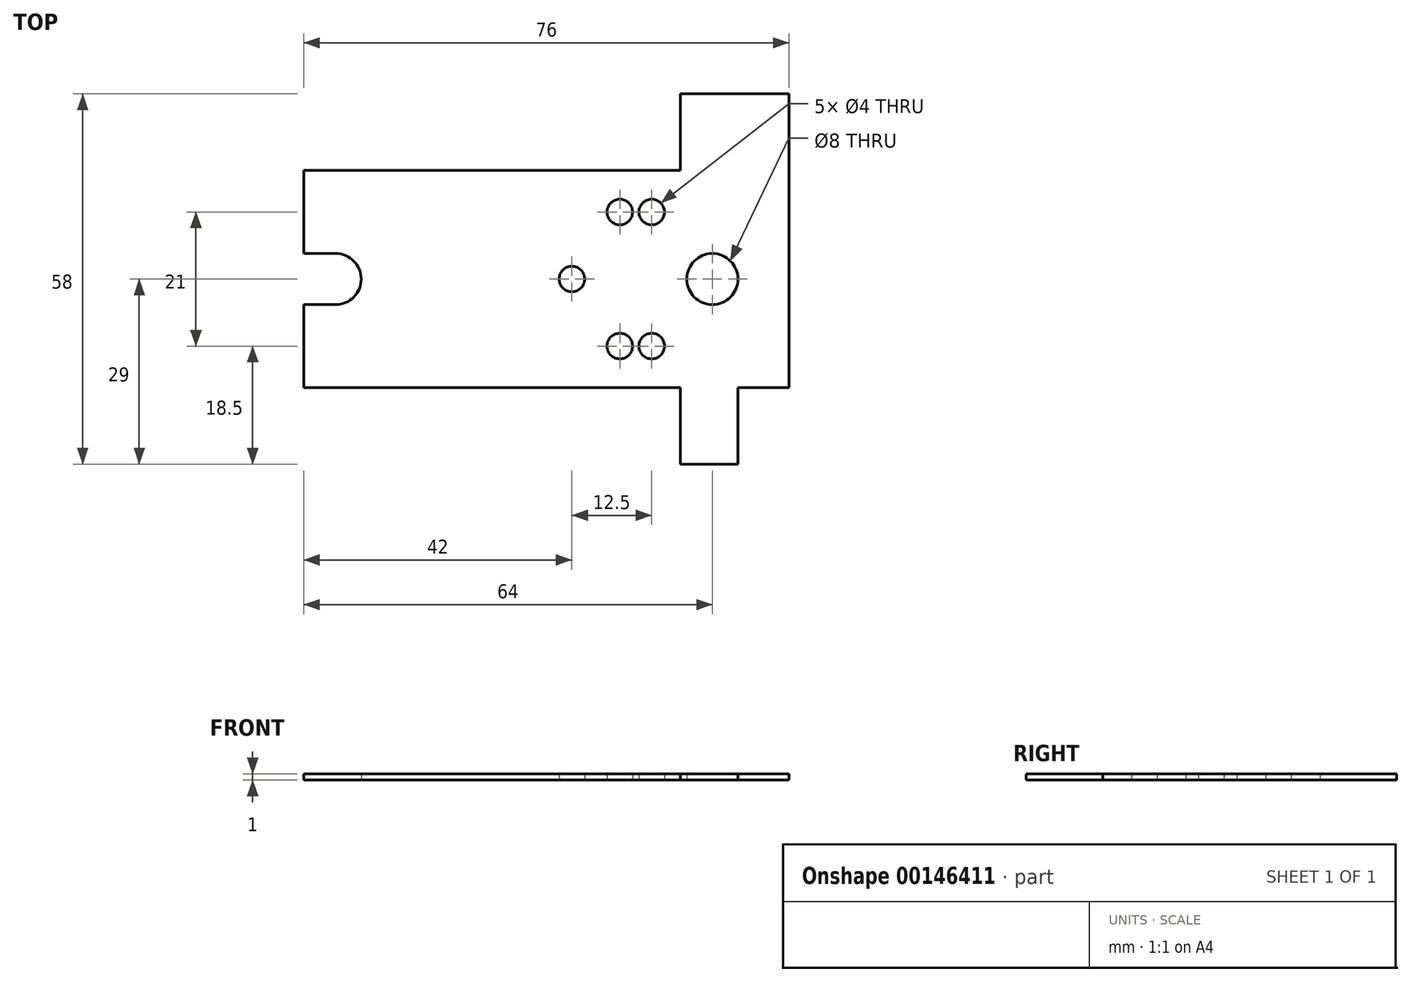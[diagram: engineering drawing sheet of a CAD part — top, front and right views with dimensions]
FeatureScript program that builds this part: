
annotation { "Feature Type Name" : "Feature", "Feature Type Description" : "" }
export const myFeature = defineFeature(function(context is Context, id is Id, definition is map)
    precondition{}
    {
        {
            var Q0;
            Q0=qCreatedBy(makeId("Top.planeOp"),FACE);
            var sketch = newSketch(context, id + "F0", { "sketchPlane" : qUnion([Q0])});
            skLineSegment(sketch, "E0.bottom", {"start": v(0, 0) * mm, "end": v(17, 0) * mm});
            skLineSegment(sketch, "E0.top", {"start": v(0, 34) * mm, "end": v(17, 34) * mm});
            skLineSegment(sketch, "E0.left", {"start": v(0, 0) * mm, "end": v(0, 34) * mm});
            skLineSegment(sketch, "E0.right", {"start": v(17, 0) * mm, "end": v(17, 34) * mm});
            skCircle(sketch, "E1", {"center": v(5, 17) * mm, "radius": 4 * mm});
            skPoint(sketch, "E2.positionSnap0", {"position": v(17, 17) * mm});
            skLineSegment(sketch, "E3.bottom", {"start": v(0, 34) * mm, "end": v(-12, 34) * mm});
            skLineSegment(sketch, "E3.top", {"start": v(0, 0) * mm, "end": v(-12, 0) * mm});
            skLineSegment(sketch, "E3.left", {"start": v(0, 34) * mm, "end": v(0, 0) * mm});
            skLineSegment(sketch, "E3.right", {"start": v(-12, 34) * mm, "end": v(-12, 0) * mm});
            skLineSegment(sketch, "E4.bottom", {"start": v(-12, 34) * mm, "end": v(-29, 34) * mm});
            skLineSegment(sketch, "E4.top", {"start": v(-12, 0) * mm, "end": v(-29, 0) * mm});
            skLineSegment(sketch, "E4.right", {"start": v(-29, 34) * mm, "end": v(-29, 0) * mm});
            skCircle(sketch, "E5", {"center": v(-17, 17) * mm, "radius": 2 * mm});
            skLineSegment(sketch, "E6", {"start": v(-19, 17) * mm, "end": v(-50, 17) * mm});
            skLineSegment(sketch, "E7.bottom", {"start": v(-4.5, 27.5) * mm, "end": v(-9.5, 27.5) * mm, "construction": true});
            skLineSegment(sketch, "E7.top", {"start": v(-4.5, 6.5) * mm, "end": v(-9.5, 6.5) * mm, "construction": true});
            skLineSegment(sketch, "E7.left", {"start": v(-4.5, 27.5) * mm, "end": v(-4.5, 6.5) * mm, "construction": true});
            skLineSegment(sketch, "E7.right", {"start": v(-9.5, 27.5) * mm, "end": v(-9.5, 6.5) * mm, "construction": true});
            skPoint(sketch, "E7.middle", {"position": v(-7, 17) * mm});
            skCircle(sketch, "E8", {"center": v(-4.5, 27.5) * mm, "radius": 2 * mm});
            skCircle(sketch, "E9", {"center": v(-9.5, 27.5) * mm, "radius": 2 * mm});
            skCircle(sketch, "E10", {"center": v(-9.5, 6.5) * mm, "radius": 2 * mm});
            skCircle(sketch, "E11", {"center": v(-4.5, 6.5) * mm, "radius": 2 * mm});
            skLineSegment(sketch, "E12.top", {"start": v(0, 46) * mm, "end": v(17, 46) * mm});
            skLineSegment(sketch, "E12.left", {"start": v(0, 34) * mm, "end": v(0, 46) * mm});
            skLineSegment(sketch, "E12.right", {"start": v(17, 34) * mm, "end": v(17, 46) * mm});
            skLineSegment(sketch, "E13.top", {"start": v(0, -12) * mm, "end": v(9, -12) * mm});
            skLineSegment(sketch, "E13.left", {"start": v(0, 0) * mm, "end": v(0, -12) * mm});
            skLineSegment(sketch, "E13.right", {"start": v(9, 0) * mm, "end": v(9, -12) * mm});
            skLineSegment(sketch, "E14.bottom", {"start": v(-29, 34) * mm, "end": v(-42, 34) * mm});
            skLineSegment(sketch, "E14.top", {"start": v(-29, 0) * mm, "end": v(-42, 0) * mm});
            skLineSegment(sketch, "E14.right", {"start": v(-42, 34) * mm, "end": v(-42, 0) * mm});
            skLineSegment(sketch, "E15.bottom", {"start": v(-42, 34) * mm, "end": v(-59, 34) * mm});
            skLineSegment(sketch, "E15.top", {"start": v(-42, 0) * mm, "end": v(-59, 0) * mm});
            skLineSegment(sketch, "E15.right", {"start": v(-59, 34) * mm, "end": v(-59, 21) * mm});
            skArc(sketch, "E16", {"start": v(-54, 13) * mm, "mid": v(-50, 17) * mm, "end": v(-54, 21) * mm});
            skLineSegment(sketch, "E17", {"start": v(-54, 13) * mm, "end": v(-59, 13) * mm});
            skLineSegment(sketch, "E18", {"start": v(-54, 21) * mm, "end": v(-59, 21) * mm});
            skLineSegment(sketch, "E19.trimOffspring", {"start": v(-59, 13) * mm, "end": v(-59, 0) * mm});
            skSolve(sketch);
        }
        {
            var Q0;
            {var subQ4=sQuery(id+"F0.wireOp",EDGE,"E15.top");Q0=makeQuery(id+"F0.imprint","IMPRINT",FACE,{"disambiguationData":[TD([[makeQuery(id+"F0.imprint","IMPRINT",EDGE,{"derivedFrom":subQ4}),-1.0]])]});}
            var Q1;
            {var subQ0=sQuery(id+"F0.wireOp",EDGE,"E15.bottom");Q1=makeQuery(id+"F0.imprint","IMPRINT",FACE,{"disambiguationData":[TD([[makeQuery(id+"F0.imprint","IMPRINT",EDGE,{"derivedFrom":subQ0}),1.0]])]});}
            var Q2;
            {var subQ5=sQuery(id+"F0.wireOp",EDGE,"E14.bottom");Q2=makeQuery(id+"F0.imprint","IMPRINT",FACE,{"disambiguationData":[TD([[makeQuery(id+"F0.imprint","IMPRINT",EDGE,{"derivedFrom":subQ5}),1.0]])]});}
            var Q3;
            {var subQ5=sQuery(id+"F0.wireOp",EDGE,"E14.top");Q3=makeQuery(id+"F0.imprint","IMPRINT",FACE,{"disambiguationData":[TD([[makeQuery(id+"F0.imprint","IMPRINT",EDGE,{"derivedFrom":subQ5}),-1.0]])]});}
            var Q4;
            {var subQ1=sQuery(id+"F0.wireOp",EDGE,"E4.bottom");Q4=makeQuery(id+"F0.imprint","IMPRINT",FACE,{"disambiguationData":[TD([[makeQuery(id+"F0.imprint","IMPRINT",EDGE,{"derivedFrom":subQ1}),1.0]])]});}
            var Q5;
            Q5=makeQuery(id+"F0.imprint","IMPRINT",FACE,{"disambiguationData":[TD([[makeQuery(id+"F0.imprint","IMPRINT",EDGE,{"derivedFrom":sQuery(id+"F0.wireOp",EDGE,"E3.bottom")}),1.0]])]});
            var Q6;
            Q6=makeQuery(id+"F0.imprint","IMPRINT",FACE,{"disambiguationData":[TD([[makeQuery(id+"F0.imprint","IMPRINT",EDGE,{"derivedFrom":sQuery(id+"F0.wireOp",EDGE,"E13.top")}),1.0]])]});
            var Q7;
            Q7=makeQuery(id+"F0.imprint","IMPRINT",FACE,{"disambiguationData":[TD([[makeQuery(id+"F0.imprint","IMPRINT",EDGE,{"derivedFrom":sQuery(id+"F0.wireOp",EDGE,"E0.top")}),1.0]])]});
            var Q8;
            {var subQ1=sQuery(id+"F0.wireOp",EDGE,"E0.right");Q8=makeQuery(id+"F0.imprint","IMPRINT",FACE,{"disambiguationData":[TD([[makeQuery(id+"F0.imprint","IMPRINT",EDGE,{"derivedFrom":subQ1}),1.0]])]});}
            extrude(context, id + "F1", {"entities" : qUnion([Q0, Q1, Q2, Q3, Q4, Q5, Q6, Q7, Q8]), "depth" : 1 * mm});
        }
    });
